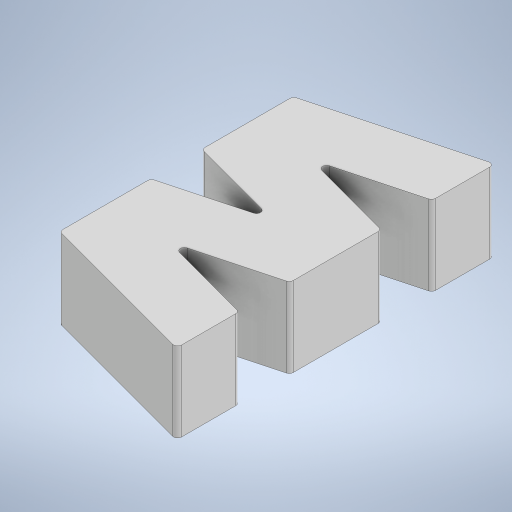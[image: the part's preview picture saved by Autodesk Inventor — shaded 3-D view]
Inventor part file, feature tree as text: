
AUTODESK INVENTOR PART (.ipt)
format: ipt  version: 2023 (Build 270158000, 158)  size: 303,616 bytes
history: native  units: mm
features: other x5, extrude x2, sketch x2, fillet x1, projected_geometry x1
ambient origin geometry x8: Origin, YZ Plane, XZ Plane, XY Plane, X Axis, Y Axis, Z Axis, Center Point
bodies: Body1 (feature_tree), Body2 (feature_tree)
feature tree (11):
  other  "contorno"
  extrude  "Extrusión1"  Depth=40.0mm
  fillet  "Empalme2"  Radius=20.0mm
  extrude  "Extrusión2"  Depth=10.0mm
  other  "Edición directa1"
  sketch  "Boceto1"  dims[d8=10.0mm d9=0.0mm d13=40.0mm d14=20.0mm]
  sketch  "Boceto2"  dims[d15=8.0mm d16=8.0mm d17=30.0deg d18=0.5mm d19=1.5mm d20=10.0mm d21=0.0mm d22=0.0mm d23=0.0mm d24=-1.5mm d25=0.0mm d26=0.0mm d27=-1.5mm]
  projected_geometry  "Contorno proyectado1"
  other  "cavidad"
  other  "Desplazar1"
  other  "Desplazar2"
